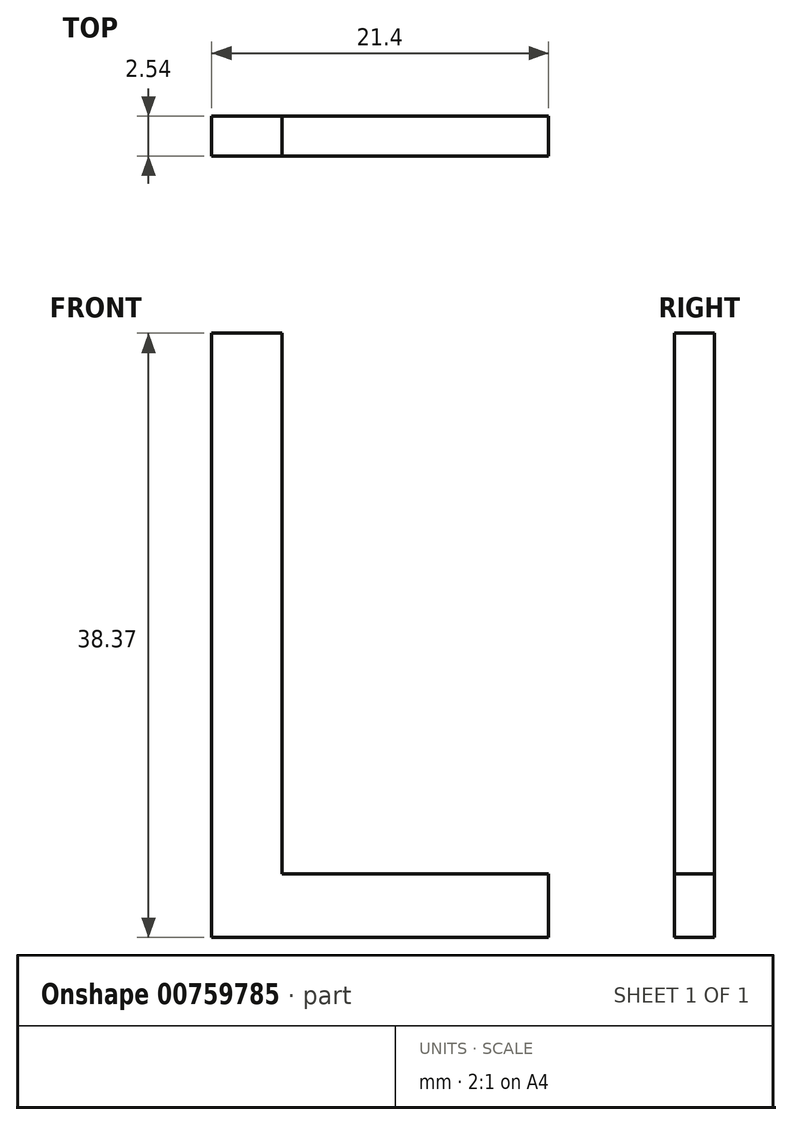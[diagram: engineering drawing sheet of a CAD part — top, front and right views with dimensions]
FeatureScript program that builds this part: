
annotation { "Feature Type Name" : "Feature", "Feature Type Description" : "" }
export const myFeature = defineFeature(function(context is Context, id is Id, definition is map)
    precondition{}
    {
        {
            var Q0;
            Q0=qCreatedBy(makeId("Front.planeOp"),FACE);
            var sketch = newSketch(context, id + "F0", { "sketchPlane" : qUnion([Q0])});
            skText(sketch, "E0", { "text": "L", "fontName": "OpenSans-Regular.ttf"});
            const initialGuessF0  = {"E0": [-0.03813, 0, 1, 0, 0.0387]};
            skSetInitialGuess(sketch, initialGuessF0);
            skSolve(sketch);
        }
        {
            var Q0;
            Q0 = qSketchRegion(id + "F0", true);
            extrude(context, id + "F1", {"entities" : qUnion([Q0]), "depth" : 2.54 * mm, "offsetDistance" : 25.4 * mm});
        }
    });
